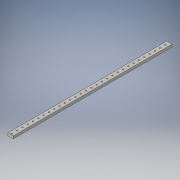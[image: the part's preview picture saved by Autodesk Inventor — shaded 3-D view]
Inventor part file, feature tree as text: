
AUTODESK INVENTOR PART (.ipt)
format: ipt  version: 2016 (Build 200138000, 138)  size: 140,288 bytes
history: native  units: in
note: dims shown in document units (in); Inventor stores cm internally (conversion verified against a paired STEP export)
features: extrude x1, sketch x1
ambient origin geometry x8: Origin, YZ Plane, XZ Plane, XY Plane, X Axis, Y Axis, Z Axis, Center Point
bodies: Solid1 (feature_tree)
feature tree (2):
  extrude  "Extrusion1"  Depth=1.0in
  sketch  "Sketch1"  dims[d0=30.0in d1=1.0in d2=0.25in d3=0.25in d4=11.811in d6=1.0in d7=0.3937in d9=1.0in d11=0.5in d12=0.0in]
